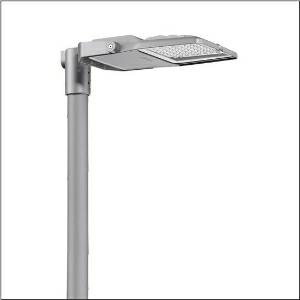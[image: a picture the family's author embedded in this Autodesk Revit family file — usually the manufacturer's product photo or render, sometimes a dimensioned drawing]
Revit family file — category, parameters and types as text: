
# Revit family: floodlight_fl_21_iq_mini___pl64_5xa7771c2e3a_b06c
name_source: partatom
category: Lighting Fixtures
units: mm (PartAtom-declared; Revit-internal decimal feet)

## family parameters
Cut with Voids When Loaded = No
Host = Face
Light Source = No
Part Type = Normal
Room Calculation Point = No
Round Connector Dimension = Use Diameter
Shared = No

## types (1)
- --- (1 x LED, 11790 lm, 87.2 W, 3000K)
    Apparent Load = 87 VA
    CIE Flux Codes = 28 80 98 100 100
    Color Rendering = 70
    Color Temperature = 3000K
    Default Elevation = 1800 mm
    Description = Floodlight FL 21 iQ mini, floodlight, primary light control with lens, of PMMA, primary optical cover: protective disc, of toughened safety glass, transparent, light distribution: PL64, light emission: direct distribution, installation type: surface-mounted, LED, High Power LED, rated luminous flux: 11.790lm, luminous efficacy: 135lm/W, light colour: 730, colour temperature: 3000K, control gear: iQ Comfort/DALI, control: Auto-Match, Temp-Guard, Lumen-Switch, Night-Set, Smart-Wire, Light-Fading, Desk-Remote (wireless, voltage-free reading and setting of iQ features in the workshop via application-optimized NFC function/RFID function), optimised constant luminous flux control (CLO 2.0), with terminal, 6-pole, mains connection: 220..240V, AC, 50/60Hz, start of lifetime: 87W, end of service life: 92W, reduction: 40W, luminaire housing, of diecast aluminium, powder-coated, Siteco® metallic grey (DB 702S), corrosivity category C5 mid according to DIN EN ISO 12944, suitable for swimming pools, chlorine-resistant, sealing non-destructively replaceable, please order mast flange separately, mast bracket, of steel, galvanised, powder-coated, Siteco® metallic grey (DB 702S), protection rating (complete): IP66, insulation class (complete): insulation class II (safety insulation), certification: CE, ENEC, VDE, protection symbol: D, impact resistance: IK08, permissible operating ambient temperature: -40..+40°C, permissible operating ambient temperature for outdoor applications: -40..+50°C, standard: DIN EN 12944, LABS conformity tested according to VDMA 24364:2018-05, packaging unit: 1 piece

Light Distribution: PL64
    Height = 70 mm
    Lamp = 1 x LED
    Lamp Light Flux = 11790 lm
    Lamp Power = 87.2 W
    Lamp count = 1
    Length = 485 mm
    Luminous efficacy = 135 lm/W
    Manufacturer = Siteco
    ModVariant = No
    Model = 5XA7771C2E3A
    Number of Poles = 1
    OnlyDefault = Yes
    Power Factor = 1
    Product Name = Floodlight FL 21 iQ mini | PL64
    Product group = floodlight | pylon annexe
    ProductGroupID = 6201
    Protection Class = Protection class II
    Protection Degree = IP 66
    RLX_Detail_Level = 1
    RLX_Emergency_Light_Flux = 0 lm
    RLX_Emergency_Type = 0
    RLX_Emergency_Type_DB = No
    RlxData = <blob elided: 101345 chars, md5=8dbda578>
    Socket = socket
    Standby Power = 0 W
    System Light Flux = 11790 lm
    System Power = 87 W
    Type Comments = factory setting: luminous flux: 100 % | dim-lin: 254 | 456 mA
    Type Image = l_1007125.jpg
    URL = http://relux.com
    VarID = @adj_188079
    Voltage = 0 V
    Weight = 0.00 kg
    Width = 337 mm

## geometry (parser evidence)
native form markers: Blend x4, Sweep x14
no freeform markers — native parametric forms only
